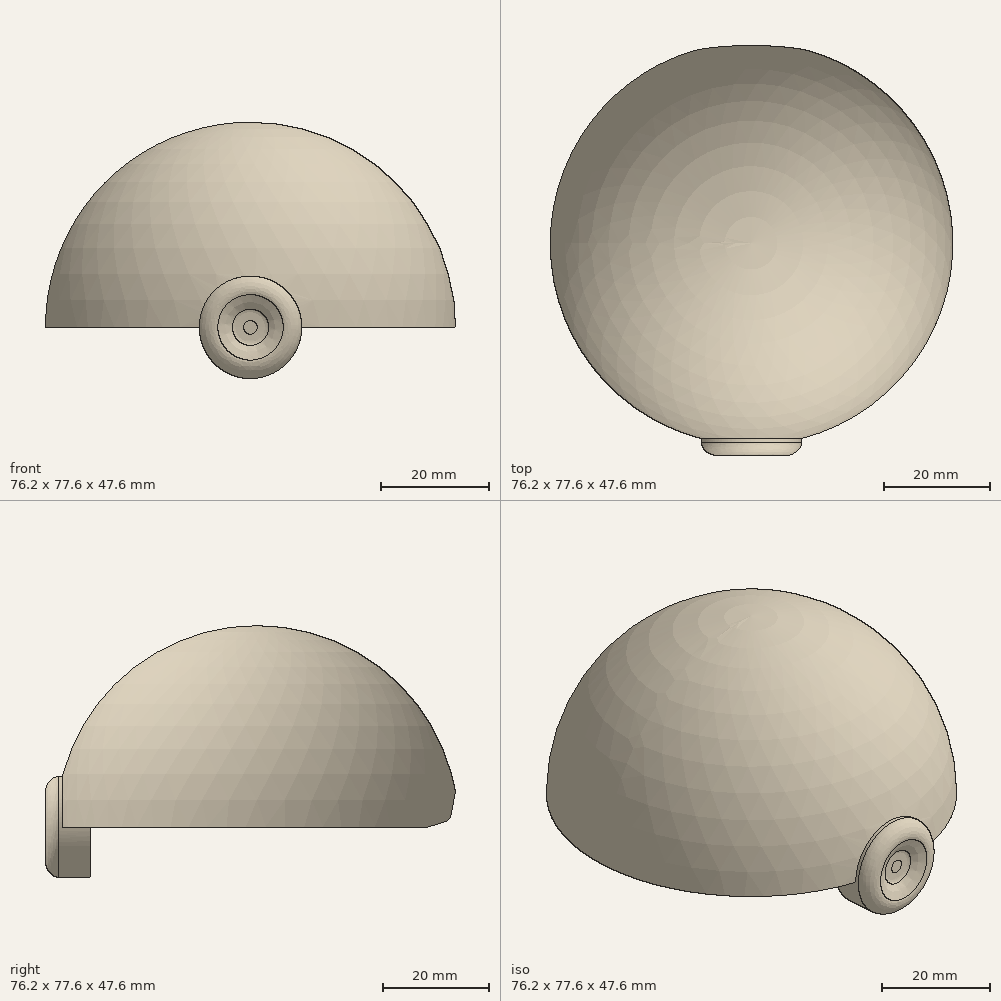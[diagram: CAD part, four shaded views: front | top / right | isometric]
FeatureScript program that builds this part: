
annotation { "Feature Type Name" : "Feature", "Feature Type Description" : "" }
export const myFeature = defineFeature(function(context is Context, id is Id, definition is map)
    precondition{}
    {
        {
            var Q0;
            Q0=qCreatedBy(makeId("Front.planeOp"),FACE);
            var sketch = newSketch(context, id + "F0", { "sketchPlane" : qUnion([Q0])});
            skArc(sketch, "E0", {"start": v(0, 38.1) * mm, "mid": v(-26.94, 26.94) * mm, "end": v(-38.1, 0) * mm});
            skLineSegment(sketch, "E1", {"start": v(-38.1, 0) * mm, "end": v(-33.02, 0) * mm});
            skLineSegment(sketch, "E2", {"start": v(0, 0) * mm, "end": v(0, 38.1) * mm, "construction": true});
            skArc(sketch, "E3.0", {"start": v(0, 33.02) * mm, "mid": v(-23.35, 23.35) * mm, "end": v(-33.02, 0) * mm});
            skLineSegment(sketch, "E4", {"start": v(0, 38.1) * mm, "end": v(0, 33.02) * mm});
            skSolve(sketch);
        }
        {
            var Q0;
            Q0=makeQuery(id+"F0.imprint","IMPRINT",FACE,{"disambiguationData":[TD([[makeQuery(id+"F0.imprint","IMPRINT",EDGE,{"derivedFrom":sQuery(id+"F0.wireOp",EDGE,"E0")}),1.0]])]});
            var Q1;
            Q1=sQuery(id+"F0.wireOp",EDGE,"E2");
            revolve(context, id + "F1", {"entities" : qUnion([Q0]), "axis" : qUnion([Q1]), "revolveType" : RevolveType.FULL});
        }
        {
            var Q0;
            Q0=qCreatedBy(makeId("Front.planeOp"),FACE);
            var sketch = newSketch(context, id + "F2", { "sketchPlane" : qUnion([Q0])});
            skCircle(sketch, "E5", {"center": v(0, 0) * mm, "radius": 9.53 * mm});
            skSolve(sketch);
        }
        {
            var Q0;
            Q0=makeQuery(id+"F2.imprint","IMPRINT",FACE,{"disambiguationData":[TD([[makeQuery(id+"F2.imprint","IMPRINT",EDGE,{"derivedFrom":sQuery(id+"F2.wireOp",EDGE,"E5")}),1.0]])]});
            extrude(context, id + "F3", {"entities" : qUnion([Q0]), "operationType" : NewBodyOperationType.ADD, "depth" : 40.64 * mm});
        }
        {
            var Q0;
            Q0=qCreatedBy(makeId("Right.planeOp"),FACE);
            var sketch = newSketch(context, id + "F4", { "sketchPlane" : qUnion([Q0])});
            skLineSegment(sketch, "E6.trimOffspring", {"start": v(33.02, 0) * mm, "end": v(38.1, 0) * mm});
            skCircle(sketch, "E7", {"center": v(35.05, 2.54) * mm, "radius": 1.65 * mm});
            skArc(sketch, "E8", {"start": v(38.1, 0) * mm, "mid": v(38.01, 2.58) * mm, "end": v(37.75, 5.15) * mm});
            skArc(sketch, "E9", {"start": v(33.02, 0) * mm, "mid": v(32.92, 2.58) * mm, "end": v(32.62, 5.15) * mm});
            skLineSegment(sketch, "E10", {"start": v(37.75, 5.15) * mm, "end": v(32.62, 5.15) * mm});
            skLineSegment(sketch, "E11", {"start": v(32.62, 5.15) * mm, "end": v(29.5, 5.15) * mm});
            skLineSegment(sketch, "E12", {"start": v(29.5, 5.15) * mm, "end": v(29.5, 0) * mm});
            skLineSegment(sketch, "E13", {"start": v(29.5, 0) * mm, "end": v(33.02, 0) * mm});
            skSolve(sketch);
        }
        {
            var Q0;
            {var subQ2=sQuery(id+"F4.wireOp",EDGE,"E11");Q0=makeQuery(id+"F4.imprint","IMPRINT",FACE,{"disambiguationData":[TD([[makeQuery(id+"F4.imprint","IMPRINT",EDGE,{"derivedFrom":subQ2}),1.0]])]});}
            var Q1;
            {var subQ1=sQuery(id+"F4.wireOp",EDGE,"E6.trimOffspring");Q1=makeQuery(id+"F4.imprint","IMPRINT",FACE,{"disambiguationData":[TD([[makeQuery(id+"F4.imprint","IMPRINT",EDGE,{"derivedFrom":subQ1}),1.0]])]});}
            extrude(context, id + "F5", {"entities" : qUnion([Q0, Q1]), "operationType" : NewBodyOperationType.REMOVE, "endBound" : BoundingType.SYMMETRIC, "oppositeDirection" : true, "depth" : 12.7 * mm});
        }
        {
            var Q0;
            Q0=qCreatedBy(makeId("Right.planeOp"),FACE);
            var sketch = newSketch(context, id + "F6", { "sketchPlane" : qUnion([Q0])});
            skArc(sketch, "E14.0", {"start": v(35.54, 0.96) * mm, "mid": v(36.28, 1.44) * mm, "end": v(36.68, 2.24) * mm});
            skLineSegment(sketch, "E15", {"start": v(37.21, 5.15) * mm, "end": v(36.68, 2.24) * mm});
            skLineSegment(sketch, "E16", {"start": v(32.4, 0) * mm, "end": v(35.54, 0.96) * mm});
            skLineSegment(sketch, "E17", {"start": v(41.38, 5.15) * mm, "end": v(41.88, -2.5) * mm});
            skLineSegment(sketch, "E18", {"start": v(41.88, -2.5) * mm, "end": v(32.72, -2.5) * mm});
            skLineSegment(sketch, "E19", {"start": v(32.72, -2.5) * mm, "end": v(32.4, 0) * mm});
            skPoint(sketch, "E20.0.1.end.orphan", {"position": v(32, 5.15) * mm});
            skLineSegment(sketch, "E21", {"start": v(37.21, 5.15) * mm, "end": v(39.19, 15.88) * mm});
            skLineSegment(sketch, "E22", {"start": v(39.19, 15.88) * mm, "end": v(41.38, 5.15) * mm});
            skSolve(sketch);
        }
        {
            var Q0;
            Q0=makeQuery(id+"F6.imprint","IMPRINT",FACE,{"disambiguationData":[TD([[makeQuery(id+"F6.imprint","IMPRINT",EDGE,{"derivedFrom":sQuery(id+"F6.wireOp",EDGE,"E14.0")}),-1.0]])]});
            extrude(context, id + "F7", {"entities" : qUnion([Q0]), "operationType" : NewBodyOperationType.REMOVE, "endBound" : BoundingType.SYMMETRIC, "oppositeDirection" : true, "depth" : 60.05 * mm});
        }
        {
            var Q0;
            Q0=qCreatedBy(makeId("Right.planeOp"),FACE);
            var sketch = newSketch(context, id + "F8", { "sketchPlane" : qUnion([Q0])});
            skArc(sketch, "E23", {"start": v(0, 33.02) * mm, "mid": v(-19.7, 26.5) * mm, "end": v(-31.62, 9.52) * mm});
            skArc(sketch, "E24", {"start": v(37.5, 6.73) * mm, "mid": v(1.43, 38.07) * mm, "end": v(-36.9, 9.53) * mm});
            skArc(sketch, "E25", {"start": v(-31.62, 9.52) * mm, "mid": v(-26.5, -19.7) * mm, "end": v(0, -33.02) * mm});
            skLineSegment(sketch, "E26", {"start": v(0, 0) * mm, "end": v(0, -33.02) * mm});
            skArc(sketch, "E27.0", {"start": v(0, 40.64) * mm, "mid": v(-24.89, 32.13) * mm, "end": v(-39.35, 10.16) * mm});
            skArc(sketch, "E28", {"start": v(-39.35, 10.16) * mm, "mid": v(-32.13, -24.89) * mm, "end": v(0, -40.64) * mm});
            skLineSegment(sketch, "E29", {"start": v(0, 33.02) * mm, "end": v(0, -33.02) * mm});
            skLineSegment(sketch, "E30", {"start": v(0, -40.64) * mm, "end": v(0, -47.28) * mm});
            skLineSegment(sketch, "E31", {"start": v(0, -47.28) * mm, "end": v(-45.95, -35) * mm});
            skLineSegment(sketch, "E32", {"start": v(-45.95, -35) * mm, "end": v(-123.55, -10.71) * mm});
            skLineSegment(sketch, "E33", {"start": v(-123.55, -10.71) * mm, "end": v(-123.55, 14.73) * mm});
            skLineSegment(sketch, "E34", {"start": v(-123.55, 14.73) * mm, "end": v(-9.75, 47.64) * mm});
            skLineSegment(sketch, "E35", {"start": v(-9.75, 47.64) * mm, "end": v(0, 40.64) * mm});
            skSolve(sketch);
        }
        {
            var Q0;
            {var subQ0=sQuery(id+"F8.wireOp",EDGE,"E23");Q0=makeQuery(id+"F8.imprint","IMPRINT",FACE,{"disambiguationData":[TD([[makeQuery(id+"F8.imprint","IMPRINT",EDGE,{"derivedFrom":subQ0}),1.0]])]});}
            var Q1;
            Q1=sQuery(id+"F8.wireOp",EDGE,"E29");
            revolve(context, id + "F9", {"operationType" : NewBodyOperationType.REMOVE, "entities" : qUnion([Q0]), "axis" : qUnion([Q1]), "revolveType" : RevolveType.FULL, "oppositeDirection" : true});
        }
        {
            var Q0;
            Q0=makeQuery(id+"F3.opExtrude","CAP_FACE",FACE,{"disambiguationData":[OSD([sQuery(id+"F2.wireOp",EDGE,"E5")])],"isStart":false});
            var sketch = newSketch(context, id + "F10", { "sketchPlane" : qUnion([Q0])});
            skCircle(sketch, "E36", {"center": v(0, 0) * mm, "radius": 3.81 * mm});
            skSolve(sketch);
        }
        {
            var Q0;
            Q0=makeQuery(id+"F10.imprint","IMPRINT",FACE,{"disambiguationData":[TD([[makeQuery(id+"F10.imprint","IMPRINT",EDGE,{"derivedFrom":sQuery(id+"F10.wireOp",EDGE,"E36")}),1.0]])]});
            extrude(context, id + "F11", {"entities" : qUnion([Q0]), "operationType" : NewBodyOperationType.REMOVE, "oppositeDirection" : true, "depth" : 2.54 * mm});
        }
        {
            var Q0;
            Q0=makeQuery(id+"F11.boolean.opBoolean","COPY",EDGE,{"derivedFrom":makeQuery(id+"F11.opExtrude","CAP_EDGE",EDGE,{"disambiguationData":[OSD([sQuery(id+"F10.wireOp",EDGE,"E36")])],"isStart":false})});
            fillet(context, id + "F12", {"entities" : qUnion([Q0]), "radius" : 2.54 * mm, "tangentPropagation" : true, "rho" : .7, "crossSection" : FilletCrossSection.CONIC, "allowEdgeOverflow" : false});
        }
        {
            var Q0;
            Q0=makeQuery(id+"F12.opFillet","BLEND_EDGE",EDGE,{"blendedFrom":[makeQuery(id+"F11.boolean.opBoolean","COPY",EDGE,{"derivedFrom":makeQuery(id+"F11.opExtrude","CAP_EDGE",EDGE,{"disambiguationData":[OSD([sQuery(id+"F10.wireOp",EDGE,"E36")])],"isStart":false})}),makeQuery(id+"F3.opExtrude","CAP_FACE",FACE,{"disambiguationData":[OSD([sQuery(id+"F2.wireOp",EDGE,"E5")])],"isStart":false})],"blendedInto":[makeQuery(id+"F3.opExtrude","CAP_FACE",FACE,{"disambiguationData":[OSD([sQuery(id+"F2.wireOp",EDGE,"E5")])],"isStart":false})]});
            fillet(context, id + "F13", {"entities" : qUnion([Q0]), "radius" : 10.16 * mm, "tangentPropagation" : true, "allowEdgeOverflow" : false});
        }
        {
            var Q0;
            {var subQ0=sQuery(id+"F2.wireOp",EDGE,"E5");Q0=makeQuery(id+"F13.opFillet","BLEND_EDGE",EDGE,{"blendedFrom":[makeQuery(id+"F12.opFillet","BLEND_EDGE",EDGE,{"blendedFrom":[makeQuery(id+"F11.boolean.opBoolean","COPY",EDGE,{"derivedFrom":makeQuery(id+"F11.opExtrude","CAP_EDGE",EDGE,{"disambiguationData":[OSD([sQuery(id+"F10.wireOp",EDGE,"E36")])],"isStart":false})}),makeQuery(id+"F3.opExtrude","CAP_FACE",FACE,{"disambiguationData":[OSD([subQ0])],"isStart":false})],"blendedInto":[makeQuery(id+"F3.opExtrude","CAP_FACE",FACE,{"disambiguationData":[OSD([subQ0])],"isStart":false})]}),makeQuery(id+"F3.opExtrude","SWEPT_FACE",FACE,{"disambiguationData":[OSD([subQ0])]})],"blendedInto":[makeQuery(id+"F3.opExtrude","SWEPT_FACE",FACE,{"disambiguationData":[OSD([subQ0])]})]});}
            fillet(context, id + "F14", {"entities" : qUnion([Q0]), "radius" : 2.54 * mm, "tangentPropagation" : true, "rho" : .3, "crossSection" : FilletCrossSection.CONIC, "allowEdgeOverflow" : false});
        }
    });
